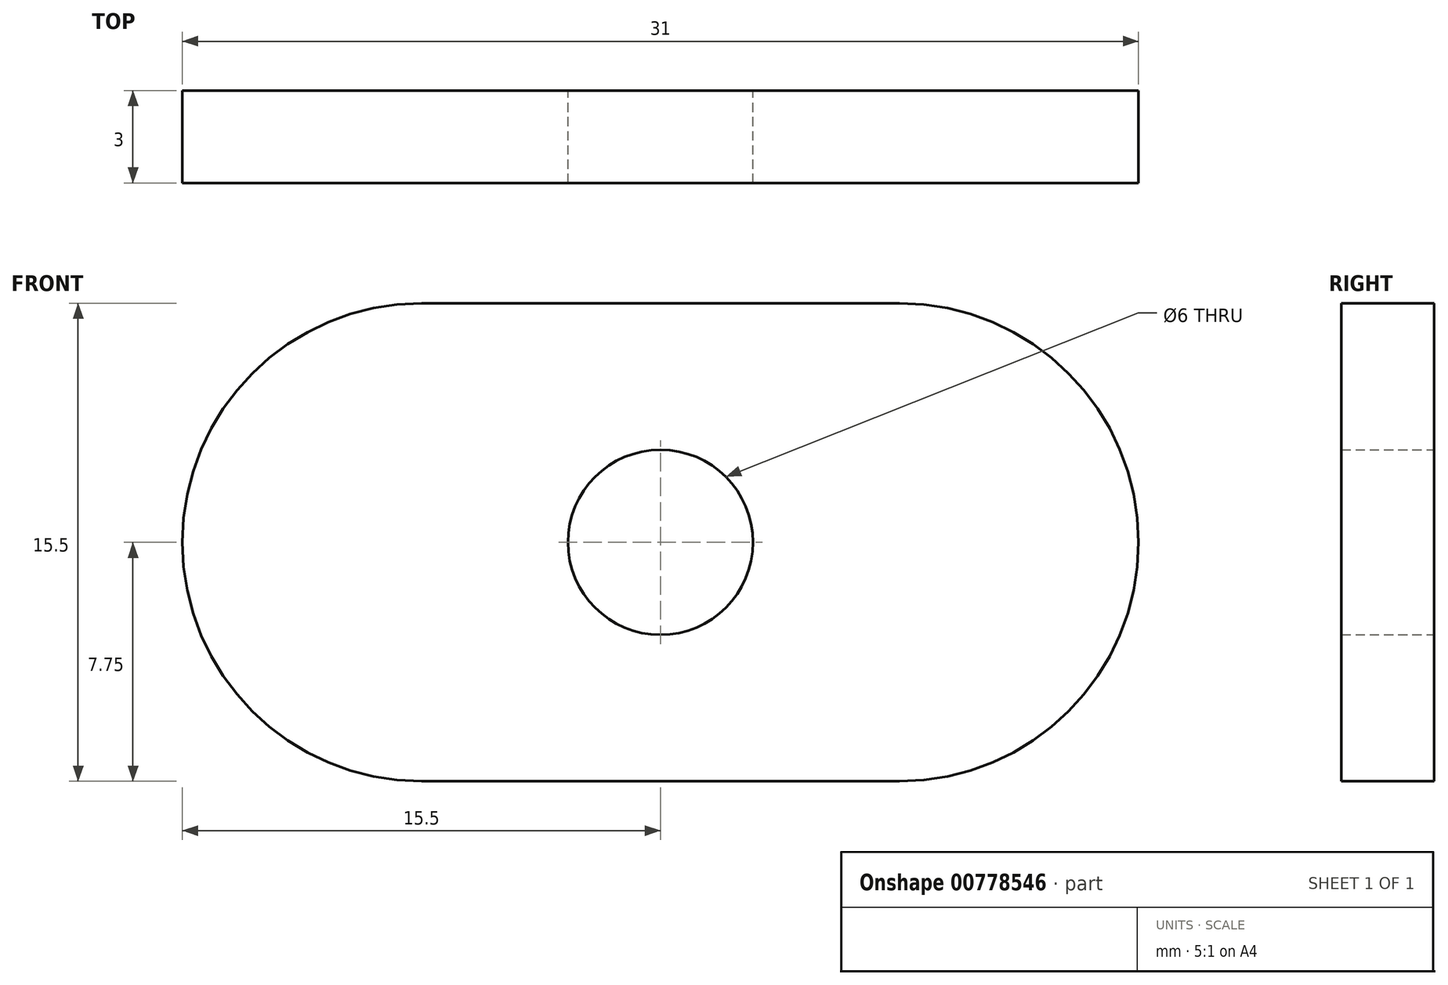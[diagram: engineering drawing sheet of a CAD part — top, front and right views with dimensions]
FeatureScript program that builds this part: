
annotation { "Feature Type Name" : "Feature", "Feature Type Description" : "" }
export const myFeature = defineFeature(function(context is Context, id is Id, definition is map)
    precondition{}
    {
        {
            var Q0;
            Q0=qCreatedBy(makeId("Front.planeOp"),FACE);
            var sketch = newSketch(context, id + "F0", { "sketchPlane" : qUnion([Q0])});
            skLineSegment(sketch, "E0.bottom", {"start": v(7.75, -7.75) * mm, "end": v(-7.75, -7.75) * mm});
            skLineSegment(sketch, "E0.top", {"start": v(7.75, 7.75) * mm, "end": v(-7.75, 7.75) * mm});
            skPoint(sketch, "E0.middle", {"position": v(0, 0) * mm});
            skArc(sketch, "E1", {"start": v(-7.75, -7.75) * mm, "mid": v(-15.5, 0) * mm, "end": v(-7.75, 7.75) * mm});
            skArc(sketch, "E2", {"start": v(7.75, 7.75) * mm, "mid": v(15.5, 0) * mm, "end": v(7.75, -7.75) * mm});
            skCircle(sketch, "E3", {"center": v(0, 0) * mm, "radius": 3 * mm});
            skSolve(sketch);
        }
        {
            var Q0;
            Q0=makeQuery(id+"F0.imprint","IMPRINT",FACE,{"disambiguationData":[TD([[makeQuery(id+"F0.imprint","IMPRINT",EDGE,{"derivedFrom":sQuery(id+"F0.wireOp",EDGE,"E0.bottom")}),-1.0]])]});
            extrude(context, id + "F1", {"entities" : qUnion([Q0]), "depth" : 3 * mm, "offsetDistance" : 25 * mm});
        }
    });
